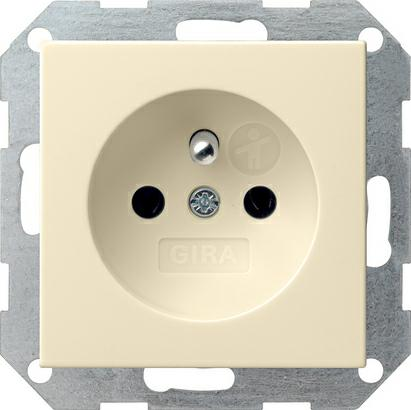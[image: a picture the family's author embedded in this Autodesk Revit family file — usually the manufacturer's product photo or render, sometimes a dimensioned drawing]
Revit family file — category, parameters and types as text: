
# Revit family: E_Cable Junction Box_MEPcontent_Spelsberg_IBTronic XL_INT-EN
name_source: partatom
category: Electrical Fixtures
revit_build: Autodesk Revit 2017 (Build: 20160225_1515(x64)
units: mm (PartAtom-declared; Revit-internal decimal feet)

## family parameters
Always vertical = Yes
Cut with Voids When Loaded = No
Maintain Annotation Orientation = Yes
OmniClass Number = 23.80.30.14.24
OmniClass Title = Junction Boxes
Part Type = Junction Box
Room Calculation Point = No
Round Connector Dimension = Use Diameter
Shared = No
Work Plane-Based = No

## types (2) — shared parameters
3D Representation = 3DGeometry
ETIM Article Class = EC000414
Height = 130 mm  [stored 0.426509 ft]
IFCExportAs = IfcJunctionBox
IFCExportType = NOTDEFINED
Length = 280 mm  [stored 0.918635 ft]
Manufacturer = Spelsberg
Manufacturer URL = http://www.spelsberg.com
Product Line = Spelsberg
Revit Version = 2017
Rotation U-Axis Correction = 0.00°
Rotation U-Axis Default Correction = 0.00°
Rotation V-Axis Correction = 0.00°
Rotation V-Axis Default Correction = 0.00°
Rotation W-Axis Correction = 0.00°
Rotation W-Axis Default Correction = 0.00°
Voltage = 230 V
Width = 252 mm  [stored 0.826772 ft]

## per-type parameters (varying)
| type | Article Description | Bottom Offset | Conduit Diameter 1 | Conduit Diameter 2 | Description | Manufacturer Art. No. | Side Distance | Side Offset |
| IBTronic XL H 185 F | Enclosure IBTronic XL H 185 F | 62 mm | 20 mm  [stored 0.0656168 ft] | 25 mm  [stored 0.082021 ft] | Enclosure IBTronic XL H 185 F | 97660401 | 25 mm  [stored 0.082021 ft] | 2 mm  [stored 0.00656168 ft] |
| IBTronic XL H 185 FE | Enclosure IBTronic XL H 185 FE | 63 mm | 16 mm  [stored 0.0524934 ft] | 19 mm  [stored 0.062336 ft] | Enclosure IBTronic XL H 185 FE | 97660402 | 24 mm  [stored 0.0787402 ft] | 7 mm  [stored 0.0229659 ft] |

note: column(s) folded — value = type name in every type: Article Type, Model

note: [stored X ft] marks values corroborated as IEEE doubles in the binary element streams (Revit-internal decimal feet)

## geometry (parser evidence)
native form markers: Sweep x17
no freeform markers — native parametric forms only
